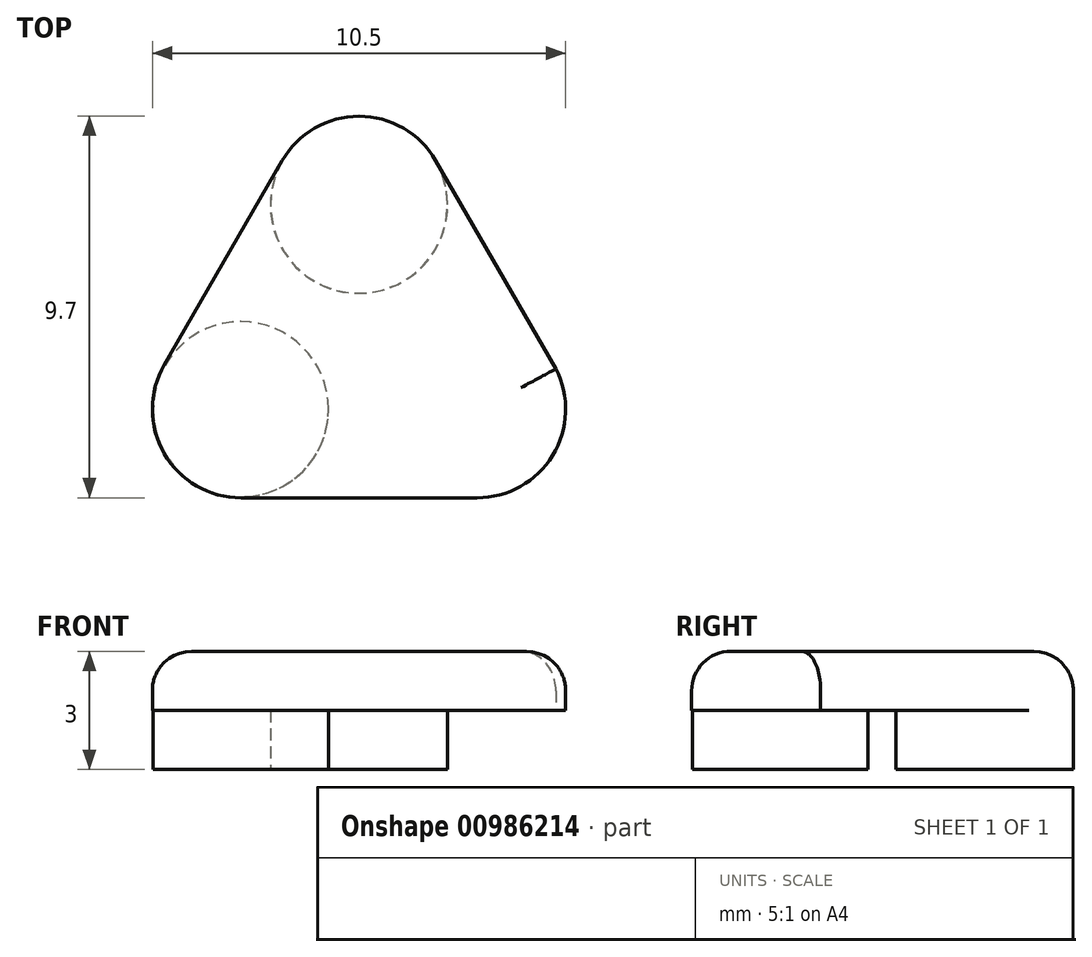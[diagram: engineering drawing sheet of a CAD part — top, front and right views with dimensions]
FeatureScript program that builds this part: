
annotation { "Feature Type Name" : "Feature", "Feature Type Description" : "" }
export const myFeature = defineFeature(function(context is Context, id is Id, definition is map)
    precondition{}
    {
        {
            var Q0;
            Q0=qCreatedBy(makeId("Top.planeOp"),FACE);
            var sketch = newSketch(context, id + "F0", { "sketchPlane" : qUnion([Q0])});
            skCircle(sketch, "E0", {"center": v(-3, 5.2) * mm, "radius": 2.25 * mm});
            skCircle(sketch, "E1", {"center": v(-6, 0) * mm, "radius": 2.25 * mm});
            skCircle(sketch, "E2", {"center": v(0, 0) * mm, "radius": 2.25 * mm});
            skLineSegment(sketch, "E3", {"start": v(-7.95, 1.13) * mm, "end": v(-4.95, 6.32) * mm});
            skLineSegment(sketch, "E4", {"start": v(-1.05, 6.32) * mm, "end": v(2, 1.03) * mm});
            skLineSegment(sketch, "E5", {"start": v(0, -2.25) * mm, "end": v(-6, -2.25) * mm});
            skSolve(sketch);
        }
        {
            var Q0;
            {var subQ0=sQuery(id+"F0.wireOp",EDGE,"E3");Q0=makeQuery(id+"F0.imprint","IMPRINT",FACE,{"disambiguationData":[TD([[makeQuery(id+"F0.imprint","IMPRINT",EDGE,{"derivedFrom":subQ0}),-1.0]])]});}
            var Q1;
            {var subQ0=sQuery(id+"F0.wireOp",EDGE,"E2");var subQ1=makeQuery(id+"F0.imprint","INTERSECT",VERTEX,{"derivedFrom":[subQ0,sQuery(id+"F0.wireOp",EDGE,"E5")]});Q1=makeQuery(id+"F0.imprint","IMPRINT",FACE,{"disambiguationData":[TD([[makeQuery(id+"F0.imprint","IMPRINT",EDGE,{"disambiguationData":[TD([[subQ1,1.0]])],"derivedFrom":subQ0}),1.0]])]});}
            var Q2;
            {var subQ0=sQuery(id+"F0.wireOp",EDGE,"E1");var subQ1=makeQuery(id+"F0.imprint","INTERSECT",VERTEX,{"derivedFrom":[subQ0,sQuery(id+"F0.wireOp",EDGE,"E3")]});Q2=makeQuery(id+"F0.imprint","IMPRINT",FACE,{"disambiguationData":[TD([[makeQuery(id+"F0.imprint","IMPRINT",EDGE,{"disambiguationData":[TD([[subQ1,-1.0]])],"derivedFrom":subQ0}),1.0]])]});}
            var Q3;
            {var subQ0=sQuery(id+"F0.wireOp",EDGE,"E0");var subQ1=makeQuery(id+"F0.imprint","INTERSECT",VERTEX,{"derivedFrom":[subQ0,sQuery(id+"F0.wireOp",EDGE,"E3")]});Q3=makeQuery(id+"F0.imprint","IMPRINT",FACE,{"disambiguationData":[TD([[makeQuery(id+"F0.imprint","IMPRINT",EDGE,{"disambiguationData":[TD([[subQ1,1.0]])],"derivedFrom":subQ0}),1.0]])]});}
            extrude(context, id + "F1", {"entities" : qUnion([Q0, Q1, Q2, Q3]), "depth" : 1.5 * mm, "offsetDistance" : 25 * mm});
        }
        {
            var Q0;
            Q0=makeQuery(id+"F1.opExtrude","CAP_FACE",FACE,{"disambiguationData":[OSD([sQuery(id+"F0.wireOp",EDGE,"E0"),sQuery(id+"F0.wireOp",EDGE,"E1"),sQuery(id+"F0.wireOp",EDGE,"E2"),sQuery(id+"F0.wireOp",EDGE,"E3"),sQuery(id+"F0.wireOp",EDGE,"E4"),sQuery(id+"F0.wireOp",EDGE,"E5")])],"isStart":true});
            var sketch = newSketch(context, id + "F2", { "sketchPlane" : qUnion([Q0])});
            skCircle(sketch, "E6", {"center": v(0, 0) * mm, "radius": 2.25 * mm});
            skCircle(sketch, "E7", {"center": v(-3, -5.2) * mm, "radius": 2.25 * mm});
            skCircle(sketch, "E8", {"center": v(-6, 0) * mm, "radius": 2.23 * mm});
            skSolve(sketch);
        }
        {
            var Q0;
            Q0=makeQuery(id+"F2.imprint","IMPRINT",FACE,{"disambiguationData":[TD([[makeQuery(id+"F2.imprint","IMPRINT",EDGE,{"derivedFrom":sQuery(id+"F2.wireOp",EDGE,"E8")}),1.0]])]});
            var Q1;
            {var subQ0=sQuery(id+"F2.wireOp",EDGE,"E6");var subQ1=makeQuery(id+"F2.imprint","INTERSECT",VERTEX,{"derivedFrom":[makeQuery(id+"F1.opExtrude","CAP_EDGE",EDGE,{"disambiguationData":[OSD([sQuery(id+"F0.wireOp",EDGE,"E5")])],"isStart":true}),subQ0]});var subQ2=makeQuery(id+"F1.opExtrude","CAP_EDGE",EDGE,{"disambiguationData":[OSD([sQuery(id+"F0.wireOp",EDGE,"E4")])],"isStart":true});var subQ3=makeQuery(id+"F2.imprint","INTERSECT",VERTEX,{"disambiguationData":[OD(1.0)],"derivedFrom":[subQ2,subQ0]});Q1=makeQuery(id+"F2.imprint","IMPRINT",FACE,{"disambiguationData":[TD([[makeQuery(id+"F2.imprint","IMPRINT",EDGE,{"disambiguationData":[TD([[subQ1,-1.0],[subQ3,1.0]])],"derivedFrom":subQ0}),1.0]])]});}
            var Q2;
            {var subQ0=sQuery(id+"F2.wireOp",EDGE,"E7");Q2=makeQuery(id+"F2.imprint","IMPRINT",FACE,{"disambiguationData":[TD([[makeQuery(id+"F2.imprint","IMPRINT",EDGE,{"disambiguationData":[OD(0.0)],"derivedFrom":subQ0}),-1.0]])]});}
            extrude(context, id + "F3", {"entities" : qUnion([Q0, Q1, Q2]), "operationType" : NewBodyOperationType.ADD, "depth" : 1.5 * mm, "offsetDistance" : 25 * mm});
        }
        {
            var Q0;
            Q0=makeQuery(id+"F1.opExtrude","CAP_EDGE",EDGE,{"disambiguationData":[OSD([sQuery(id+"F0.wireOp",EDGE,"E3")])],"isStart":false});
            var Q1;
            Q1=makeQuery(id+"F1.opExtrude","CAP_EDGE",EDGE,{"disambiguationData":[OSD([sQuery(id+"F0.wireOp",EDGE,"E0")])],"isStart":false});
            var Q2;
            Q2=makeQuery(id+"F1.opExtrude","CAP_EDGE",EDGE,{"disambiguationData":[OSD([sQuery(id+"F0.wireOp",EDGE,"E4")])],"isStart":false});
            var Q3;
            Q3=makeQuery(id+"F1.opExtrude","CAP_EDGE",EDGE,{"disambiguationData":[OSD([sQuery(id+"F0.wireOp",EDGE,"E2")])],"isStart":false});
            var Q4;
            Q4=makeQuery(id+"F1.opExtrude","CAP_EDGE",EDGE,{"disambiguationData":[OSD([sQuery(id+"F0.wireOp",EDGE,"E5")])],"isStart":false});
            var Q5;
            Q5=makeQuery(id+"F1.opExtrude","CAP_EDGE",EDGE,{"disambiguationData":[OSD([sQuery(id+"F0.wireOp",EDGE,"E1")])],"isStart":false});
            fillet(context, id + "F4", {"entities" : qUnion([Q0, Q1, Q2, Q3, Q4, Q5]), "radius" : 1 * mm, "tangentPropagation" : true, "allowEdgeOverflow" : false});
        }
    });
